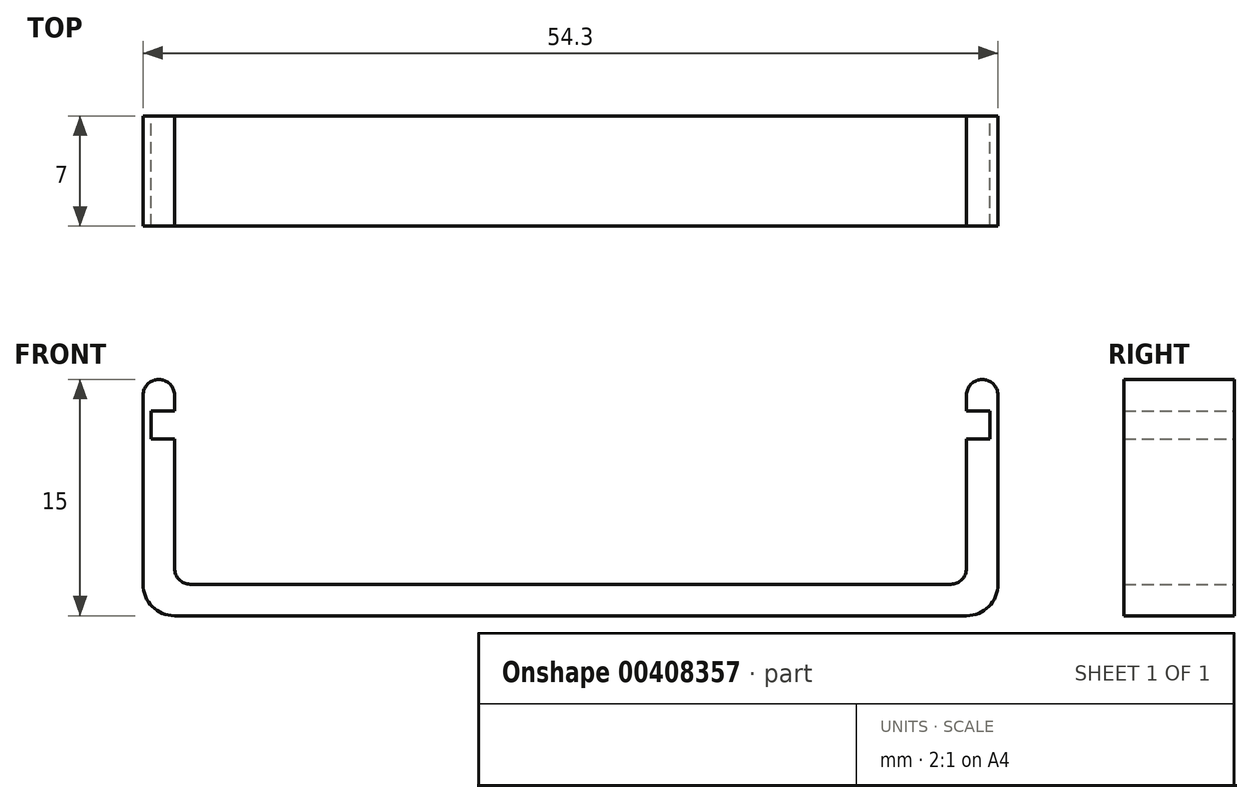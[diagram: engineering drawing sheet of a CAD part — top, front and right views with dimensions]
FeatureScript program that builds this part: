
annotation { "Feature Type Name" : "Feature", "Feature Type Description" : "" }
export const myFeature = defineFeature(function(context is Context, id is Id, definition is map)
    precondition{}
    {
        {
            var Q0;
            Q0=qCreatedBy(makeId("Front.planeOp"),FACE);
            var sketch = newSketch(context, id + "F0", { "sketchPlane" : qUnion([Q0])});
            skLineSegment(sketch, "E0", {"start": v(-23.55, -13.3) * mm, "end": v(-23.55, -28.3) * mm});
            skLineSegment(sketch, "E1", {"start": v(-23.55, -28.3) * mm, "end": v(30.75, -28.3) * mm});
            skLineSegment(sketch, "E2", {"start": v(30.75, -28.3) * mm, "end": v(30.75, -13.3) * mm});
            skLineSegment(sketch, "E3", {"start": v(30.75, -13.3) * mm, "end": v(28.75, -13.3) * mm});
            skLineSegment(sketch, "E4", {"start": v(28.75, -13.3) * mm, "end": v(28.75, -15.3) * mm});
            skLineSegment(sketch, "E5", {"start": v(28.75, -15.3) * mm, "end": v(30.25, -15.3) * mm});
            skLineSegment(sketch, "E6", {"start": v(30.25, -15.3) * mm, "end": v(30.25, -17.08) * mm});
            skLineSegment(sketch, "E7", {"start": v(30.25, -17.08) * mm, "end": v(28.75, -17.08) * mm});
            skLineSegment(sketch, "E8", {"start": v(28.75, -17.08) * mm, "end": v(28.75, -26.3) * mm});
            skLineSegment(sketch, "E9", {"start": v(28.75, -26.3) * mm, "end": v(-21.55, -26.3) * mm});
            skLineSegment(sketch, "E10", {"start": v(-21.55, -26.3) * mm, "end": v(-21.55, -17.08) * mm});
            skLineSegment(sketch, "E11", {"start": v(-21.55, -17.08) * mm, "end": v(-23.05, -17.08) * mm});
            skLineSegment(sketch, "E12", {"start": v(-23.05, -17.08) * mm, "end": v(-23.05, -15.3) * mm});
            skLineSegment(sketch, "E13", {"start": v(-23.05, -15.3) * mm, "end": v(-21.55, -15.3) * mm});
            skLineSegment(sketch, "E14", {"start": v(-21.55, -15.3) * mm, "end": v(-21.55, -13.3) * mm});
            skLineSegment(sketch, "E15", {"start": v(-21.55, -13.3) * mm, "end": v(-23.55, -13.3) * mm});
            skSolve(sketch);
        }
        {
            var Q0;
            Q0=makeQuery(id+"F0.imprint","IMPRINT",FACE,{"disambiguationData":[TD([[makeQuery(id+"F0.imprint","IMPRINT",EDGE,{"derivedFrom":sQuery(id+"F0.wireOp",EDGE,"E0")}),1.0]])]});
            extrude(context, id + "F1", {"entities" : qUnion([Q0]), "depth" : 7 * mm});
        }
        {
            var Q0;
            Q0=makeQuery(id+"F1.opExtrude","SWEPT_EDGE",EDGE,{"disambiguationData":[OSD([sQuery(id+"F0.wireOp",EDGE,"E0"),sQuery(id+"F0.wireOp",EDGE,"E1")])]});
            var Q1;
            Q1=makeQuery(id+"F1.opExtrude","SWEPT_EDGE",EDGE,{"disambiguationData":[OSD([sQuery(id+"F0.wireOp",EDGE,"E1"),sQuery(id+"F0.wireOp",EDGE,"E2")])]});
            fillet(context, id + "F2", {"entities" : qUnion([Q0, Q1]), "radius" : 2 * mm, "tangentPropagation" : true, "allowEdgeOverflow" : false});
        }
        {
            var Q0;
            Q0=makeQuery(id+"F1.opExtrude","SWEPT_EDGE",EDGE,{"disambiguationData":[OSD([sQuery(id+"F0.wireOp",EDGE,"E9"),sQuery(id+"F0.wireOp",EDGE,"E10")])]});
            var Q1;
            Q1=makeQuery(id+"F1.opExtrude","SWEPT_EDGE",EDGE,{"disambiguationData":[OSD([sQuery(id+"F0.wireOp",EDGE,"E8"),sQuery(id+"F0.wireOp",EDGE,"E9")])]});
            fillet(context, id + "F3", {"entities" : qUnion([Q0, Q1]), "radius" : 1 * mm, "tangentPropagation" : true, "allowEdgeOverflow" : false});
        }
        {
            var Q0;
            Q0=makeQuery(id+"F1.opExtrude","SWEPT_EDGE",EDGE,{"disambiguationData":[OSD([sQuery(id+"F0.wireOp",EDGE,"E0"),sQuery(id+"F0.wireOp",EDGE,"E15")])]});
            var Q1;
            Q1=makeQuery(id+"F1.opExtrude","SWEPT_EDGE",EDGE,{"disambiguationData":[OSD([sQuery(id+"F0.wireOp",EDGE,"E2"),sQuery(id+"F0.wireOp",EDGE,"E3")])]});
            var Q2;
            Q2=makeQuery(id+"F1.opExtrude","SWEPT_EDGE",EDGE,{"disambiguationData":[OSD([sQuery(id+"F0.wireOp",EDGE,"E14"),sQuery(id+"F0.wireOp",EDGE,"E15")])]});
            var Q3;
            Q3=makeQuery(id+"F1.opExtrude","SWEPT_EDGE",EDGE,{"disambiguationData":[OSD([sQuery(id+"F0.wireOp",EDGE,"E3"),sQuery(id+"F0.wireOp",EDGE,"E4")])]});
            fillet(context, id + "F4", {"entities" : qUnion([Q0, Q1, Q2, Q3]), "radius" : 1 * mm, "tangentPropagation" : true, "allowEdgeOverflow" : false});
        }
    });
